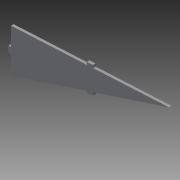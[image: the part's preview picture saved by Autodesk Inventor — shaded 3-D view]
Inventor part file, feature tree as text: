
AUTODESK INVENTOR PART (.ipt)
format: ipt  version: 2015 (Build 190159000, 159)  size: 112,640 bytes
history: native  units: in
note: dims shown in document units (in); Inventor stores cm internally (conversion verified against a paired STEP export)
features: sketch x3, extrude x2
ambient origin geometry x8: Origin, YZ Plane, XZ Plane, XY Plane, X Axis, Y Axis, Z Axis, Center Point
bodies: Solid1 (feature_tree)
feature tree (5):
  extrude  "Extrusion1"  Depth=0.125in TaperAngle=0.0deg
  extrude  "Extrusion5"  Depth=0.3in
  sketch  "Sketch6"  dims[d37=0.15in d38=0.125in d39=0.15in d40=0.3in d41=0.125in d42=0.15in d44=0.3in d45=0.125in d46=0.125in d47=0.0in d48=0.639in]
  sketch  "Sketch1"  dims[d0=2.084in d2=0.125in d3=0.0in]
  sketch  "Sketch5"  dims[d34=0.1036in d36=0.3in]
